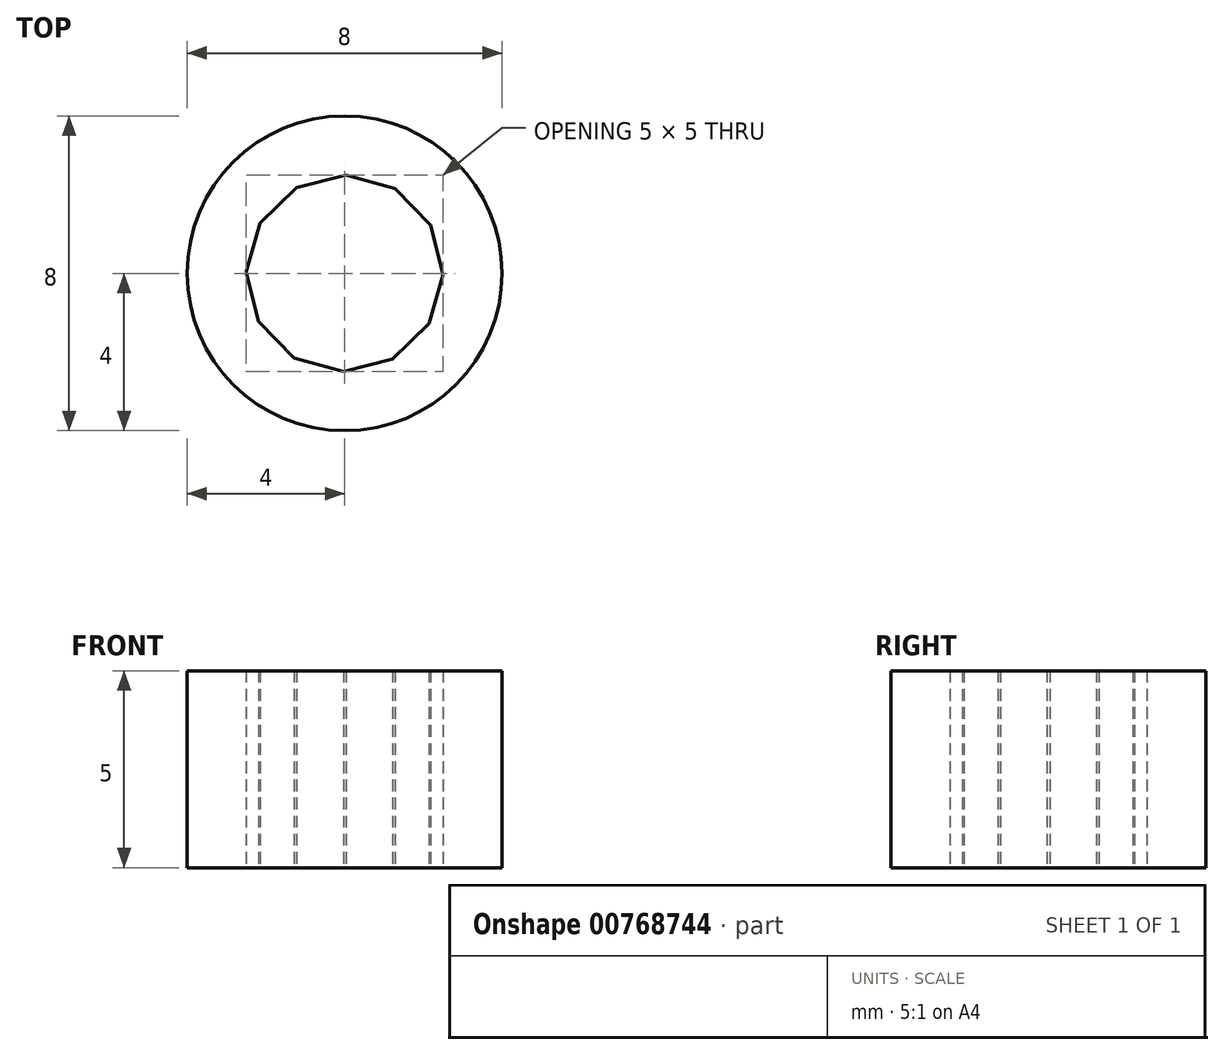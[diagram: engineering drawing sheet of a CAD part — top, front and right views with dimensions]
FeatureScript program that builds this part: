
annotation { "Feature Type Name" : "Feature", "Feature Type Description" : "" }
export const myFeature = defineFeature(function(context is Context, id is Id, definition is map)
    precondition{}
    {
        {
            var Q0;
            Q0=qCreatedBy(makeId("Top.planeOp"),FACE);
            var sketch = newSketch(context, id + "F0", { "sketchPlane" : qUnion([Q0])});
            skCircle(sketch, "E0.cCircle", {"center": v(0, 0) * mm, "radius": 2.5 * mm, "construction": true});
            skLineSegment(sketch, "E0.0", {"start": v(-1.28, -2.15) * mm, "end": v(-2.18, -1.22) * mm});
            skLineSegment(sketch, "E0.1", {"start": v(-2.18, -1.22) * mm, "end": v(-2.5, 0.03) * mm});
            skLineSegment(sketch, "E0.2", {"start": v(-2.5, 0.03) * mm, "end": v(-2.15, 1.28) * mm});
            skLineSegment(sketch, "E0.3", {"start": v(-2.15, 1.28) * mm, "end": v(-1.22, 2.18) * mm});
            skLineSegment(sketch, "E0.4", {"start": v(-1.22, 2.18) * mm, "end": v(0.03, 2.5) * mm});
            skLineSegment(sketch, "E0.5", {"start": v(0.03, 2.5) * mm, "end": v(1.28, 2.15) * mm});
            skLineSegment(sketch, "E0.6", {"start": v(1.28, 2.15) * mm, "end": v(2.18, 1.22) * mm});
            skLineSegment(sketch, "E0.7", {"start": v(2.18, 1.22) * mm, "end": v(2.5, -0.03) * mm});
            skLineSegment(sketch, "E0.8", {"start": v(2.5, -0.03) * mm, "end": v(2.15, -1.28) * mm});
            skLineSegment(sketch, "E0.9", {"start": v(2.15, -1.28) * mm, "end": v(1.22, -2.18) * mm});
            skLineSegment(sketch, "E0.10", {"start": v(1.22, -2.18) * mm, "end": v(-0.03, -2.5) * mm});
            skLineSegment(sketch, "E0.11", {"start": v(-0.03, -2.5) * mm, "end": v(-1.28, -2.15) * mm});
            skCircle(sketch, "E1", {"center": v(0, 0) * mm, "radius": 4 * mm});
            skSolve(sketch);
        }
        {
            var Q0;
            Q0 = qSketchRegion(id + "F0", true);
            extrude(context, id + "F1", {"entities" : qUnion([Q0]), "depth" : 5 * mm, "offsetDistance" : 25 * mm});
        }
    });
